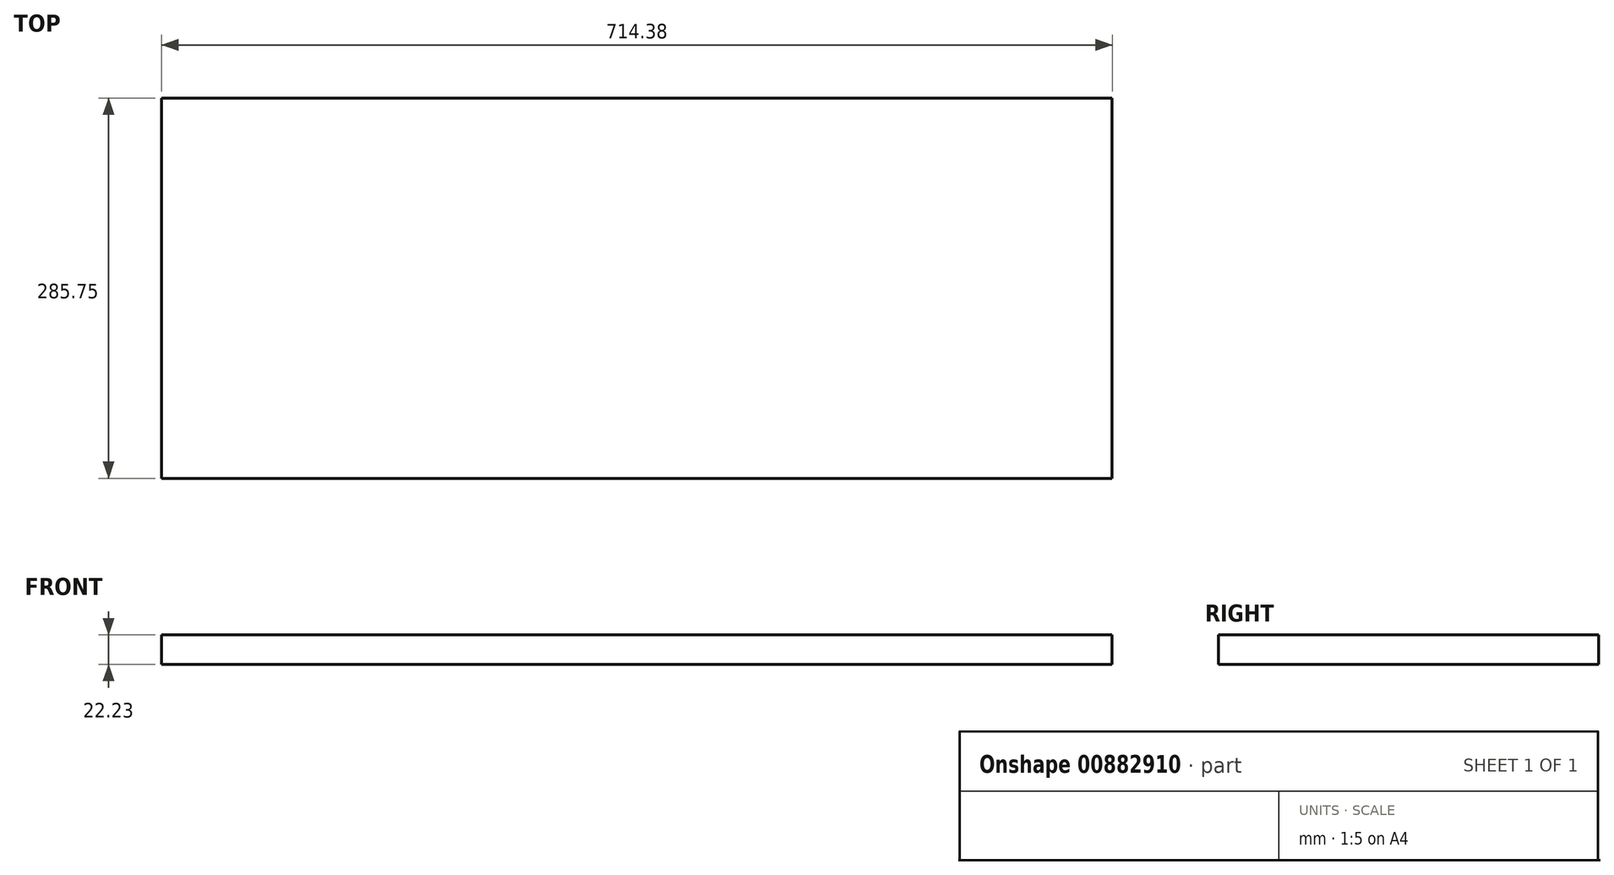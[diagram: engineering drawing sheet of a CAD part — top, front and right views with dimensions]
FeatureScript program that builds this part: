
annotation { "Feature Type Name" : "Feature", "Feature Type Description" : "" }
export const myFeature = defineFeature(function(context is Context, id is Id, definition is map)
    precondition{}
    {
        {
            var Q0;
            Q0=qCreatedBy(makeId("Right.planeOp"),FACE);
            var sketch = newSketch(context, id + "F0", { "sketchPlane" : qUnion([Q0])});
            skLineSegment(sketch, "E0.bottom", {"start": v(0, 0) * mm, "end": v(285.75, 0) * mm});
            skLineSegment(sketch, "E0.top", {"start": v(0, -22.22) * mm, "end": v(285.75, -22.22) * mm});
            skLineSegment(sketch, "E0.left", {"start": v(0, 0) * mm, "end": v(0, -22.22) * mm});
            skLineSegment(sketch, "E0.right", {"start": v(285.75, 0) * mm, "end": v(285.75, -22.22) * mm});
            skSolve(sketch);
        }
        {
            var Q0;
            Q0=makeQuery(id+"F0.imprint","IMPRINT",FACE,{"disambiguationData":[TD([[makeQuery(id+"F0.imprint","IMPRINT",EDGE,{"derivedFrom":sQuery(id+"F0.wireOp",EDGE,"E0.bottom")}),-1.0]])]});
            extrude(context, id + "F1", {"entities" : qUnion([Q0]), "depth" : 714.38 * mm, "offsetDistance" : 25.4 * mm});
        }
    });
